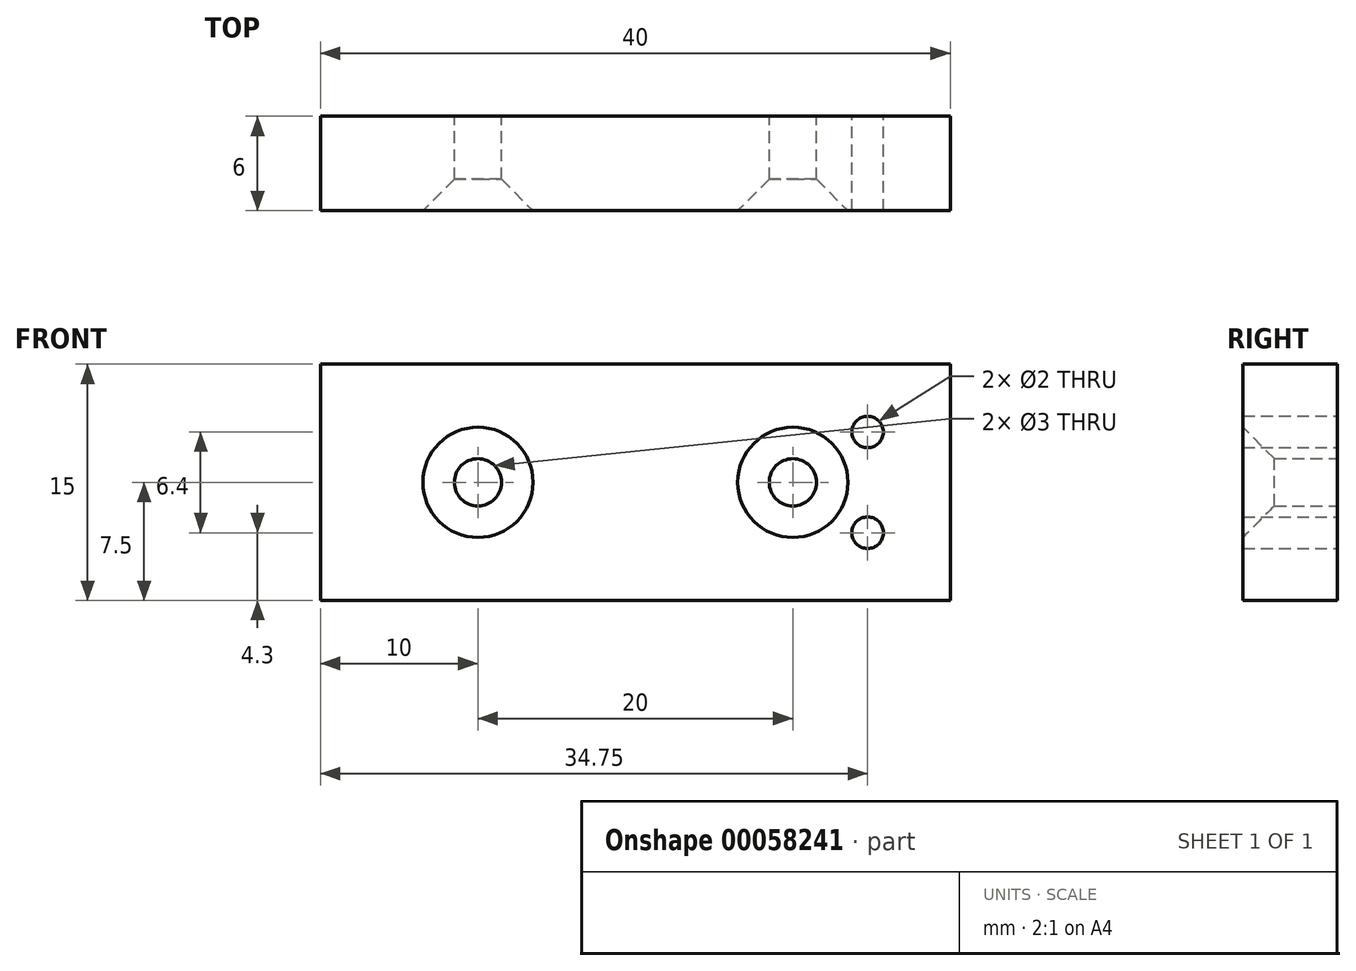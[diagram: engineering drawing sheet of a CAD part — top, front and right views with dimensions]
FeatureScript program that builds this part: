
annotation { "Feature Type Name" : "Feature", "Feature Type Description" : "" }
export const myFeature = defineFeature(function(context is Context, id is Id, definition is map)
    precondition{}
    {
        {
            var Q0;
            Q0=qCreatedBy(makeId("Front.planeOp"),FACE);
            var sketch = newSketch(context, id + "F0", { "sketchPlane" : qUnion([Q0])});
            skLineSegment(sketch, "E0.bottom", {"start": v(20, 7.5) * mm, "end": v(-20, 7.5) * mm});
            skLineSegment(sketch, "E0.top", {"start": v(20, -7.5) * mm, "end": v(-20, -7.5) * mm});
            skLineSegment(sketch, "E0.left", {"start": v(20, 7.5) * mm, "end": v(20, -7.5) * mm});
            skLineSegment(sketch, "E0.right", {"start": v(-20, 7.5) * mm, "end": v(-20, -7.5) * mm});
            skPoint(sketch, "E0.middle", {"position": v(0, 0) * mm});
            skLineSegment(sketch, "E1", {"start": v(-20, 0) * mm, "end": v(0, 0) * mm, "construction": true});
            skLineSegment(sketch, "E2", {"start": v(0, 7.5) * mm, "end": v(0, 0) * mm, "construction": true});
            skCircle(sketch, "E3", {"center": v(-10, 0) * mm, "radius": 1.5 * mm});
            skCircle(sketch, "E4", {"center": v(14.75, 3.2) * mm, "radius": 1 * mm});
            skCircle(sketch, "E5", {"center": v(14.75, -3.2) * mm, "radius": 1 * mm});
            skCircle(sketch, "E6", {"center": v(10, 0) * mm, "radius": 1.5 * mm});
            skSolve(sketch);
        }
        {
            var Q0;
            Q0=qSketchRegion(id+"F0",true);
            extrude(context, id + "F1", {"entities" : qUnion([Q0]), "depth" : 6 * mm});
        }
        {
            var Q0;
            Q0=makeQuery(id+"F1.opExtrude","CAP_EDGE",EDGE,{"disambiguationData":[OSD([sQuery(id+"F0.wireOp",EDGE,"E3")])],"isStart":false});
            var Q1;
            Q1=makeQuery(id+"F1.opExtrude","CAP_EDGE",EDGE,{"disambiguationData":[OSD([sQuery(id+"F0.wireOp",EDGE,"E6")])],"isStart":false});
            chamfer(context, id + "F2", {"entities" : qUnion([Q0, Q1]), "width" : 2 * mm, "tangentPropagation" : true});
        }
    });
